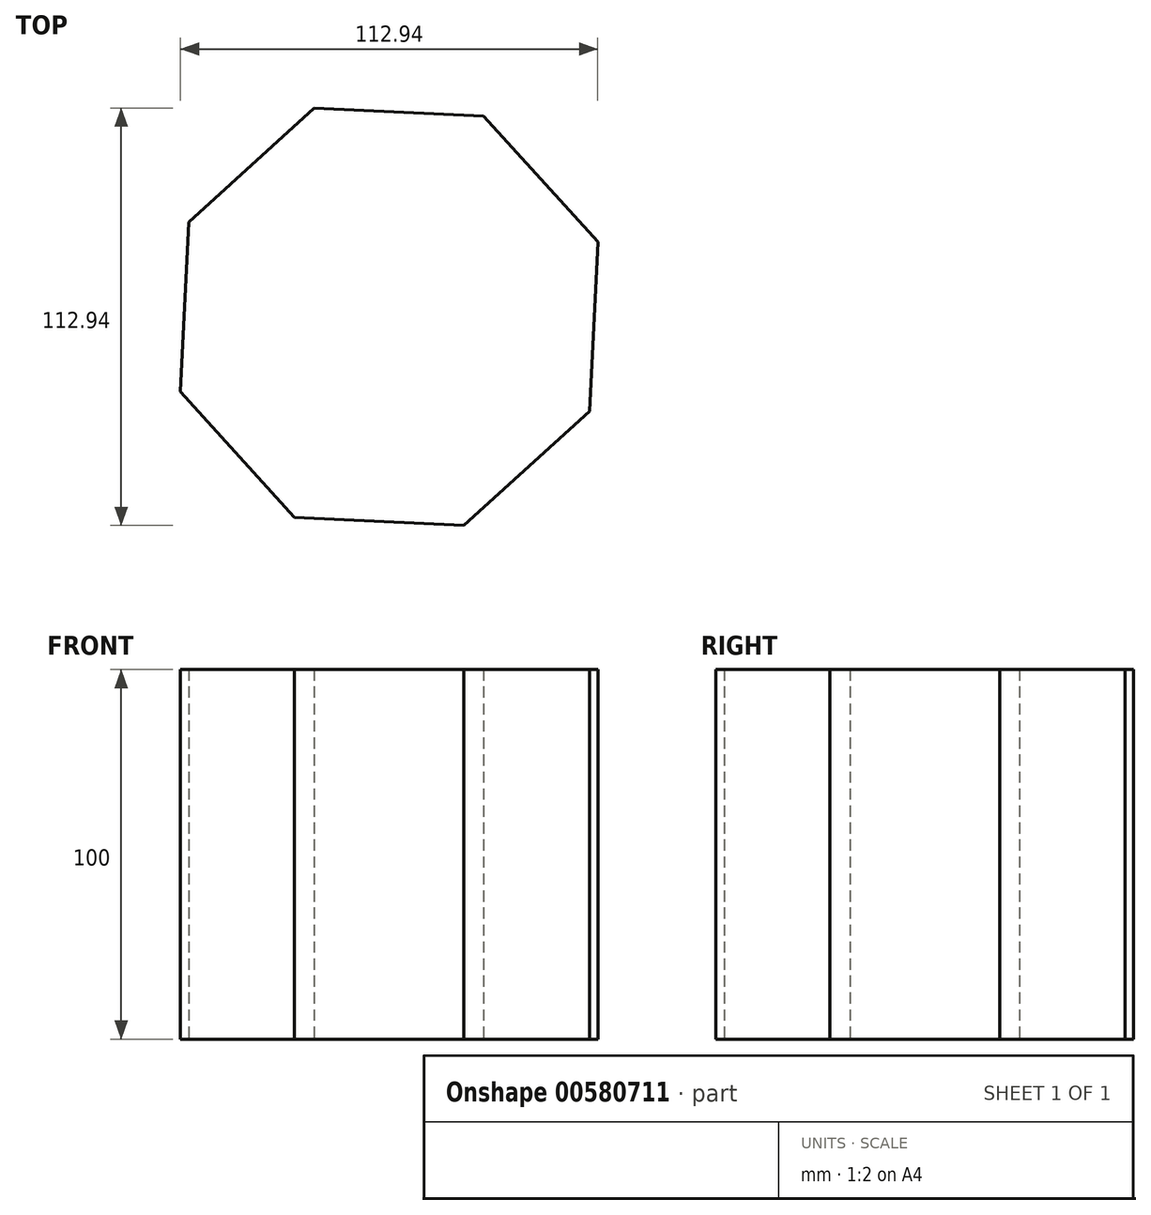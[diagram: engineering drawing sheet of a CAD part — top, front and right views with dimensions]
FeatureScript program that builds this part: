
annotation { "Feature Type Name" : "Feature", "Feature Type Description" : "" }
export const myFeature = defineFeature(function(context is Context, id is Id, definition is map)
    precondition{}
    {
        {
            var Q0;
            Q0=qCreatedBy(makeId("Top.planeOp"),FACE);
            var sketch = newSketch(context, id + "F0", { "sketchPlane" : qUnion([Q0])});
            skCircle(sketch, "E0.cCircle", {"center": v(0, 0) * mm, "radius": 60 * mm, "construction": true});
            skLineSegment(sketch, "E0.0", {"start": v(54.26, -25.6) * mm, "end": v(20.26, -56.47) * mm});
            skLineSegment(sketch, "E0.1", {"start": v(20.26, -56.47) * mm, "end": v(-25.6, -54.26) * mm});
            skLineSegment(sketch, "E0.2", {"start": v(-25.6, -54.26) * mm, "end": v(-56.47, -20.26) * mm});
            skLineSegment(sketch, "E0.3", {"start": v(-56.47, -20.26) * mm, "end": v(-54.26, 25.6) * mm});
            skLineSegment(sketch, "E0.4", {"start": v(-54.26, 25.6) * mm, "end": v(-20.26, 56.47) * mm});
            skLineSegment(sketch, "E0.5", {"start": v(-20.26, 56.47) * mm, "end": v(25.6, 54.26) * mm});
            skLineSegment(sketch, "E0.6", {"start": v(25.6, 54.26) * mm, "end": v(56.47, 20.26) * mm});
            skLineSegment(sketch, "E0.7", {"start": v(56.47, 20.26) * mm, "end": v(54.26, -25.6) * mm});
            skSolve(sketch);
        }
        {
            var Q0;
            Q0=makeQuery(id+"F0.imprint","IMPRINT",FACE,{"disambiguationData":[TD([[makeQuery(id+"F0.imprint","IMPRINT",EDGE,{"derivedFrom":sQuery(id+"F0.wireOp",EDGE,"E0.0")}),-1.0]])]});
            extrude(context, id + "F1", {"entities" : qUnion([Q0]), "depth" : 100 * mm, "offsetDistance" : 25 * mm});
        }
    });
